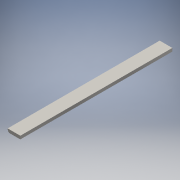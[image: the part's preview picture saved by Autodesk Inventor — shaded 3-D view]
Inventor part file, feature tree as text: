
AUTODESK INVENTOR PART (.ipt)
format: ipt  version: 2018 (Build 220112000, 112)  size: 101,888 bytes
history: native  units: in
note: dims shown in document units (in); Inventor stores cm internally (conversion verified against a paired STEP export)
features: reference x3, other x3, sketch x1, plane x1, extrude x1
ambient origin geometry x8: Origin, YZ Plane, XZ Plane, XY Plane, X Axis, Y Axis, Z Axis, Center Point
bodies: Solid1 (feature_tree)
feature tree (9):
  sketch  "Sketch1"  dims[d0=1.5in d1=0.5in d2=1.0in d3=0.0in d4=4.0in]
  plane  "Work Plane1"
  extrude  "Extrusion1"  Depth=0.5in
  reference  "Reference1"
  reference  "Reference2"
  reference  "Reference3"
  other  "<userpath>\Documents\Caleb School 2017-2018\GroupProject\HydraulicsCJE.iam"
  other  "HydraulicsCJE.iam"
  other  "Hydraulic ShaftCJE:1"
